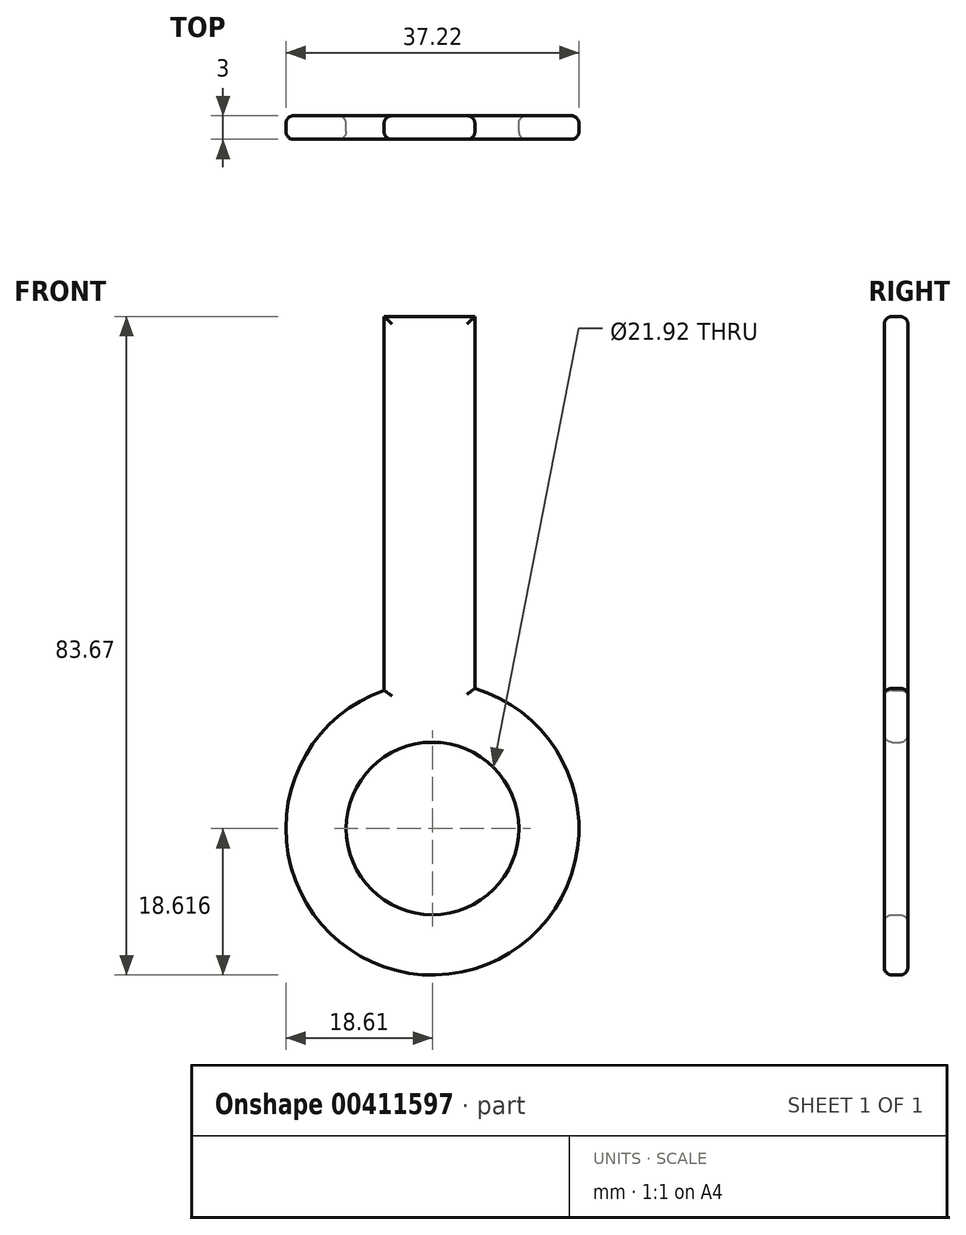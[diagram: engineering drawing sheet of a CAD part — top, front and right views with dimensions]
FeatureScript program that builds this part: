
annotation { "Feature Type Name" : "Feature", "Feature Type Description" : "" }
export const myFeature = defineFeature(function(context is Context, id is Id, definition is map)
    precondition{}
    {
        {
            var Q0;
            Q0=qCreatedBy(makeId("Front.planeOp"),FACE);
            var sketch = newSketch(context, id + "F0", { "sketchPlane" : qUnion([Q0])});
            skCircle(sketch, "E0", {"center": v(0, -65.05) * mm, "radius": 10.96 * mm});
            skCircle(sketch, "E1", {"center": v(0, -65.05) * mm, "radius": 18.61 * mm});
            skPoint(sketch, "E2.startSnap0", {"position": v(0, -32.53) * mm});
            skLineSegment(sketch, "E3", {"start": v(-6.15, -47.49) * mm, "end": v(-6.15, 0) * mm});
            skLineSegment(sketch, "E4", {"start": v(5.4, -47.24) * mm, "end": v(5.4, 0) * mm});
            skLineSegment(sketch, "E5", {"start": v(5.4, 0) * mm, "end": v(-6.15, 0) * mm});
            skSolve(sketch);
        }
        {
            var Q0;
            {var subQ0=sQuery(id+"F0.wireOp",EDGE,"E3");Q0=makeQuery(id+"F0.imprint","IMPRINT",FACE,{"disambiguationData":[TD([[makeQuery(id+"F0.imprint","IMPRINT",EDGE,{"derivedFrom":subQ0}),-1.0]])]});}
            var Q1;
            Q1=makeQuery(id+"F0.imprint","IMPRINT",FACE,{"disambiguationData":[TD([[makeQuery(id+"F0.imprint","IMPRINT",EDGE,{"derivedFrom":sQuery(id+"F0.wireOp",EDGE,"E0")}),-1.0]])]});
            extrude(context, id + "F1", {"entities" : qUnion([Q0, Q1]), "depth" : 3 * mm});
        }
        {
            var Q0;
            Q0=makeQuery(id+"F1.opExtrude","CAP_FACE",FACE,{"disambiguationData":[OSD([sQuery(id+"F0.wireOp",EDGE,"E0"),sQuery(id+"F0.wireOp",EDGE,"E1"),sQuery(id+"F0.wireOp",EDGE,"E3"),sQuery(id+"F0.wireOp",EDGE,"E4"),sQuery(id+"F0.wireOp",EDGE,"E5")])],"isStart":false});
            var Q1;
            Q1=makeQuery(id+"F1.opExtrude","CAP_EDGE",EDGE,{"disambiguationData":[OSD([sQuery(id+"F0.wireOp",EDGE,"E5")])],"isStart":false});
            var Q2;
            Q2=makeQuery(id+"F1.opExtrude","CAP_FACE",FACE,{"disambiguationData":[OSD([sQuery(id+"F0.wireOp",EDGE,"E0"),sQuery(id+"F0.wireOp",EDGE,"E1"),sQuery(id+"F0.wireOp",EDGE,"E3"),sQuery(id+"F0.wireOp",EDGE,"E4"),sQuery(id+"F0.wireOp",EDGE,"E5")])],"isStart":true});
            fillet(context, id + "F2", {"entities" : qUnion([Q0, Q1, Q2]), "radius" : 1 * mm, "tangentPropagation" : true, "allowEdgeOverflow" : false});
        }
    });
